# Revit family: LSVB96
name_source: partatom
category: Lighting Fixtures
units: mm (PartAtom-declared; Revit-internal decimal feet)

## family parameters
Always vertical = Yes
Cut with Voids When Loaded = No
Host = Ceiling
Light Source = Yes
OmniClass Number = 23.80.70.11
OmniClass Title = Luminaries for Internal Lighting
Part Type = Normal
Room Calculation Point = No
Round Connector Dimension = Use Diameter
Shared = No

## types (5) — shared parameters
Assembly Code = D5020200
Color Filter = 16777215
Description = LED Sealed Vapour B
Dimming Lamp Color Temperature Shift = <None>
Emit from Line Length = 7' - 9 3/4"
Housing Finish = Metal - Viscor - White
Lamp = LED
Length = 7' - 9 3/4"
Lens Finsih = Polycarbonate - Viscor - Frosted Round
Manufacturer = VISIONEERING by VISCOR
Model = LSVB96
Tilt Angle = 90.00°
URL = https://www.viscor.com
Voltage = 120 V
Width = 0' - 3 7/8"

## per-type parameters (varying)
| type | Apparent Load | Lamp Wattage | Photometric Web File |
| LSVB96-LED840K080LUNV | 58 VA | 58 VA | LSVB96-LED840K080LUNV.ies |
| LSVB96-LED840K120LUNV | 87 VA | 87 VA | LSVB96-LED840K120LUNV.ies |
| LSVB96-LED840K100LUNV | 79 VA | 79 VA | LSVB96-LED840K100LUNV.ies |
| LSVB96-LED840K070LUNV | 53 VA | 53 VA | LSVB48-LED840K070LUNV.IES |
| LSVB96-LED840K140LUNV | 106 VA | 106 VA | LSVB96-LED840K140LUNV.ies |

## geometry (parser evidence)
native form markers: Sweep x2
no freeform markers — native parametric forms only
